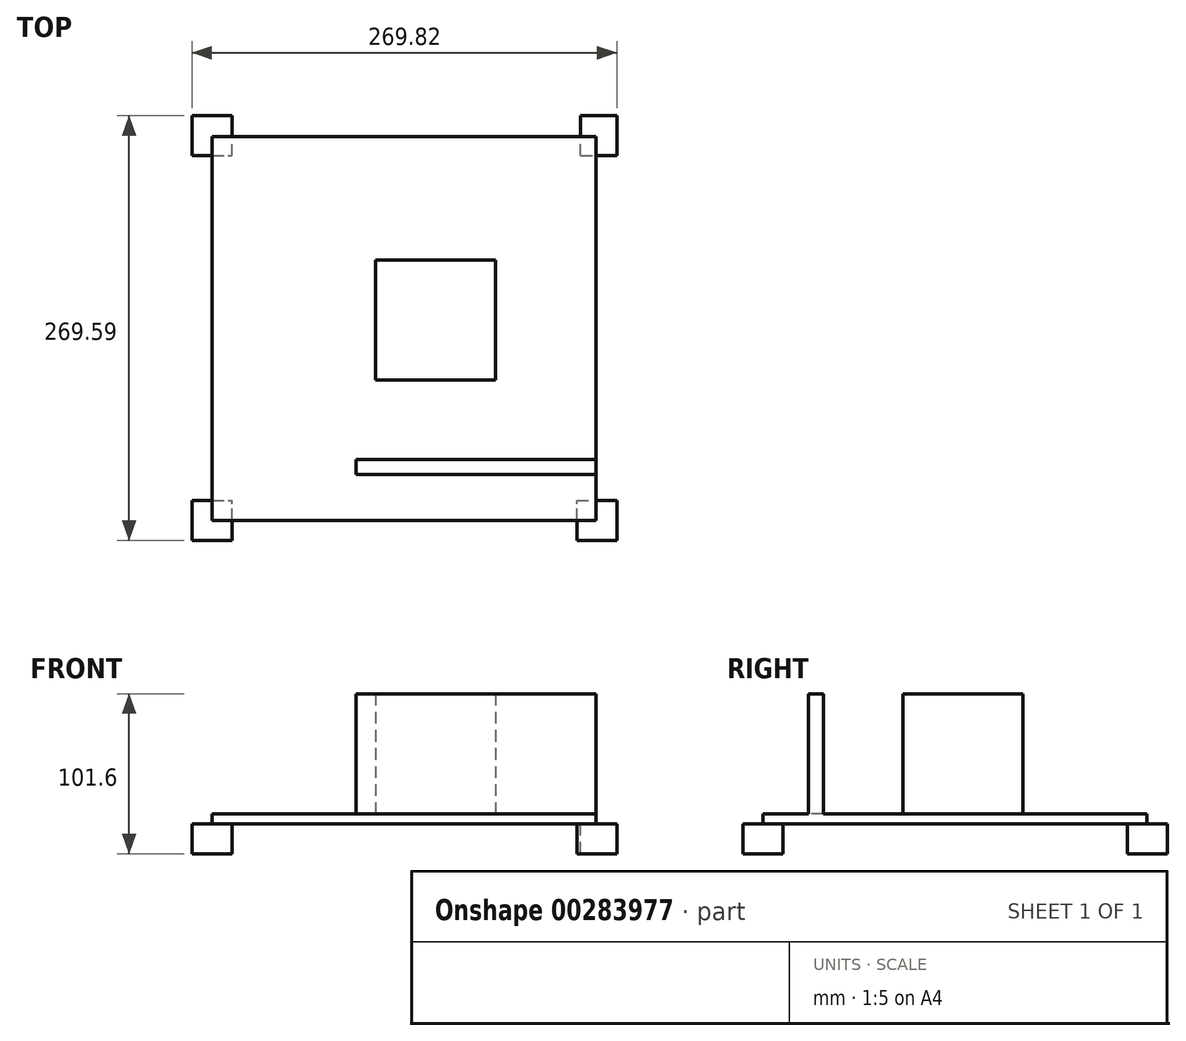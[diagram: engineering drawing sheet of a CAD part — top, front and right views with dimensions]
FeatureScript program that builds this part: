
annotation { "Feature Type Name" : "Feature", "Feature Type Description" : "" }
export const myFeature = defineFeature(function(context is Context, id is Id, definition is map)
    precondition{}
    {
        {
            var Q0;
            Q0=qCreatedBy(makeId("Top.planeOp"),FACE);
            var sketch = newSketch(context, id + "F0", { "sketchPlane" : qUnion([Q0])});
            skLineSegment(sketch, "E0.bottom", {"start": v(0, 0) * mm, "end": v(243.84, 0) * mm});
            skLineSegment(sketch, "E0.top", {"start": v(0, 243.84) * mm, "end": v(243.84, 243.84) * mm});
            skLineSegment(sketch, "E0.left", {"start": v(0, 0) * mm, "end": v(0, 243.84) * mm});
            skLineSegment(sketch, "E0.right", {"start": v(243.84, 0) * mm, "end": v(243.84, 243.84) * mm});
            skSolve(sketch);
        }
        {
            var Q0;
            Q0=makeQuery(id+"F0.imprint","IMPRINT",FACE,{"disambiguationData":[TD([[makeQuery(id+"F0.imprint","IMPRINT",EDGE,{"derivedFrom":sQuery(id+"F0.wireOp",EDGE,"E0.bottom")}),1.0]])]});
            extrude(context, id + "F1", {"entities" : qUnion([Q0]), "depth" : 6.35 * mm});
        }
        {
            var Q0;
            Q0=makeQuery(id+"F1.opExtrude","CAP_FACE",FACE,{"disambiguationData":[OSD([sQuery(id+"F0.wireOp",EDGE,"E0.bottom"),sQuery(id+"F0.wireOp",EDGE,"E0.top"),sQuery(id+"F0.wireOp",EDGE,"E0.left"),sQuery(id+"F0.wireOp",EDGE,"E0.right")])],"isStart":false});
            var sketch = newSketch(context, id + "F2", { "sketchPlane" : qUnion([Q0])});
            skLineSegment(sketch, "E1.bottom", {"start": v(103.8, 165.2) * mm, "end": v(180, 165.2) * mm});
            skLineSegment(sketch, "E1.top", {"start": v(103.8, 89) * mm, "end": v(180, 89) * mm});
            skLineSegment(sketch, "E1.left", {"start": v(103.8, 165.2) * mm, "end": v(103.8, 89) * mm});
            skLineSegment(sketch, "E1.right", {"start": v(180, 165.2) * mm, "end": v(180, 89) * mm});
            skSolve(sketch);
        }
        {
            var Q0;
            Q0=makeQuery(id+"F2.imprint","IMPRINT",FACE,{"disambiguationData":[TD([[makeQuery(id+"F2.imprint","IMPRINT",EDGE,{"derivedFrom":sQuery(id+"F2.wireOp",EDGE,"E1.bottom")}),-1.0]])]});
            extrude(context, id + "F3", {"entities" : qUnion([Q0]), "operationType" : NewBodyOperationType.ADD, "depth" : 76.2 * mm});
        }
        {
            var Q0;
            Q0=makeQuery(id+"F1.opExtrude","CAP_FACE",FACE,{"disambiguationData":[OSD([sQuery(id+"F0.wireOp",EDGE,"E0.bottom"),sQuery(id+"F0.wireOp",EDGE,"E0.top"),sQuery(id+"F0.wireOp",EDGE,"E0.left"),sQuery(id+"F0.wireOp",EDGE,"E0.right")])],"isStart":true});
            var sketch = newSketch(context, id + "F4", { "sketchPlane" : qUnion([Q0])});
            skLineSegment(sketch, "E2.bottom", {"start": v(-12.7, 12.7) * mm, "end": v(12.7, 12.7) * mm});
            skLineSegment(sketch, "E2.top", {"start": v(-12.7, -12.7) * mm, "end": v(12.7, -12.7) * mm});
            skLineSegment(sketch, "E2.left", {"start": v(-12.7, 12.7) * mm, "end": v(-12.7, -12.7) * mm});
            skLineSegment(sketch, "E2.right", {"start": v(12.7, 12.7) * mm, "end": v(12.7, -12.7) * mm});
            skLineSegment(sketch, "E3.bottom", {"start": v(231.72, 12.7) * mm, "end": v(257.12, 12.7) * mm});
            skLineSegment(sketch, "E3.top", {"start": v(231.72, -12.7) * mm, "end": v(257.12, -12.7) * mm});
            skLineSegment(sketch, "E3.left", {"start": v(231.72, 12.7) * mm, "end": v(231.72, -12.7) * mm});
            skLineSegment(sketch, "E3.right", {"start": v(257.12, 12.7) * mm, "end": v(257.12, -12.7) * mm});
            skLineSegment(sketch, "E4.bottom", {"start": v(234.11, -231.5) * mm, "end": v(257.12, -231.5) * mm});
            skLineSegment(sketch, "E4.top", {"start": v(234.11, -256.9) * mm, "end": v(257.12, -256.9) * mm});
            skLineSegment(sketch, "E4.left", {"start": v(234.11, -231.5) * mm, "end": v(234.11, -256.9) * mm});
            skLineSegment(sketch, "E4.right", {"start": v(257.12, -231.5) * mm, "end": v(257.12, -256.9) * mm});
            skLineSegment(sketch, "E5.bottom", {"start": v(-12.7, -231.5) * mm, "end": v(12.7, -231.5) * mm});
            skLineSegment(sketch, "E5.top", {"start": v(-12.7, -256.9) * mm, "end": v(12.7, -256.9) * mm});
            skLineSegment(sketch, "E5.left", {"start": v(-12.7, -231.5) * mm, "end": v(-12.7, -256.9) * mm});
            skLineSegment(sketch, "E5.right", {"start": v(12.7, -231.5) * mm, "end": v(12.7, -256.9) * mm});
            skSolve(sketch);
        }
        {
            var Q0;
            {var subQ1=sQuery(id+"F4.wireOp",EDGE,"E2.bottom");Q0=makeQuery(id+"F4.imprint","IMPRINT",FACE,{"disambiguationData":[TD([[makeQuery(id+"F4.imprint","IMPRINT",EDGE,{"derivedFrom":subQ1}),-1.0]])]});}
            var Q1;
            {var subQ0=sQuery(id+"F4.wireOp",EDGE,"E2.right");var subQ1=sQuery(id+"F4.wireOp",EDGE,"E2.top");var subQ2=makeQuery(id+"F4.imprint","INTERSECT",VERTEX,{"derivedFrom":[subQ1,subQ0]});Q1=makeQuery(id+"F4.imprint","IMPRINT",FACE,{"disambiguationData":[TD([[makeQuery(id+"F4.imprint","IMPRINT",EDGE,{"disambiguationData":[TD([[subQ2,1.0]])],"derivedFrom":subQ1}),1.0]])]});}
            var Q2;
            {var subQ1=sQuery(id+"F4.wireOp",EDGE,"E3.bottom");Q2=makeQuery(id+"F4.imprint","IMPRINT",FACE,{"disambiguationData":[TD([[makeQuery(id+"F4.imprint","IMPRINT",EDGE,{"derivedFrom":subQ1}),-1.0]])]});}
            var Q3;
            {var subQ0=sQuery(id+"F4.wireOp",EDGE,"E3.left");var subQ1=sQuery(id+"F4.wireOp",EDGE,"E3.top");var subQ2=makeQuery(id+"F4.imprint","INTERSECT",VERTEX,{"derivedFrom":[subQ1,subQ0]});Q3=makeQuery(id+"F4.imprint","IMPRINT",FACE,{"disambiguationData":[TD([[makeQuery(id+"F4.imprint","IMPRINT",EDGE,{"disambiguationData":[TD([[subQ2,-1.0]])],"derivedFrom":subQ1}),1.0]])]});}
            var Q4;
            {var subQ0=sQuery(id+"F4.wireOp",EDGE,"E5.right");var subQ1=sQuery(id+"F4.wireOp",EDGE,"E5.bottom");var subQ2=makeQuery(id+"F4.imprint","INTERSECT",VERTEX,{"derivedFrom":[subQ1,subQ0]});Q4=makeQuery(id+"F4.imprint","IMPRINT",FACE,{"disambiguationData":[TD([[makeQuery(id+"F4.imprint","IMPRINT",EDGE,{"disambiguationData":[TD([[subQ2,1.0]])],"derivedFrom":subQ1}),-1.0]])]});}
            var Q5;
            {var subQ1=sQuery(id+"F4.wireOp",EDGE,"E5.top");Q5=makeQuery(id+"F4.imprint","IMPRINT",FACE,{"disambiguationData":[TD([[makeQuery(id+"F4.imprint","IMPRINT",EDGE,{"derivedFrom":subQ1}),1.0]])]});}
            var Q6;
            {var subQ6=sQuery(id+"F4.wireOp",EDGE,"E4.top");Q6=makeQuery(id+"F4.imprint","IMPRINT",FACE,{"disambiguationData":[TD([[makeQuery(id+"F4.imprint","IMPRINT",EDGE,{"derivedFrom":subQ6}),1.0]])]});}
            var Q7;
            {var subQ0=sQuery(id+"F4.wireOp",EDGE,"E4.left");var subQ1=sQuery(id+"F4.wireOp",EDGE,"E4.bottom");var subQ2=makeQuery(id+"F4.imprint","INTERSECT",VERTEX,{"derivedFrom":[subQ1,subQ0]});Q7=makeQuery(id+"F4.imprint","IMPRINT",FACE,{"disambiguationData":[TD([[makeQuery(id+"F4.imprint","IMPRINT",EDGE,{"disambiguationData":[TD([[subQ2,-1.0]])],"derivedFrom":subQ1}),-1.0]])]});}
            extrude(context, id + "F5", {"entities" : qUnion([Q0, Q1, Q2, Q3, Q4, Q5, Q6, Q7]), "operationType" : NewBodyOperationType.ADD, "depth" : 19.05 * mm});
        }
        {
            var Q0;
            Q0=makeQuery(id+"F1.opExtrude","CAP_FACE",FACE,{"disambiguationData":[OSD([sQuery(id+"F0.wireOp",EDGE,"E0.bottom"),sQuery(id+"F0.wireOp",EDGE,"E0.top"),sQuery(id+"F0.wireOp",EDGE,"E0.left"),sQuery(id+"F0.wireOp",EDGE,"E0.right")])],"isStart":false});
            var sketch = newSketch(context, id + "F6", { "sketchPlane" : qUnion([Q0])});
            skLineSegment(sketch, "E6.bottom", {"start": v(91.44, 38.44) * mm, "end": v(243.84, 38.44) * mm});
            skLineSegment(sketch, "E6.top", {"start": v(91.44, 28.92) * mm, "end": v(243.84, 28.92) * mm});
            skLineSegment(sketch, "E6.left", {"start": v(91.44, 38.44) * mm, "end": v(91.44, 28.92) * mm});
            skLineSegment(sketch, "E6.right", {"start": v(243.84, 38.44) * mm, "end": v(243.84, 28.92) * mm});
            skSolve(sketch);
        }
        {
            var Q0;
            Q0=makeQuery(id+"F6.imprint","IMPRINT",FACE,{"disambiguationData":[TD([[makeQuery(id+"F6.imprint","IMPRINT",EDGE,{"derivedFrom":sQuery(id+"F6.wireOp",EDGE,"E6.bottom")}),-1.0]])]});
            extrude(context, id + "F7", {"entities" : qUnion([Q0]), "operationType" : NewBodyOperationType.ADD, "depth" : 76.2 * mm});
        }
    });
